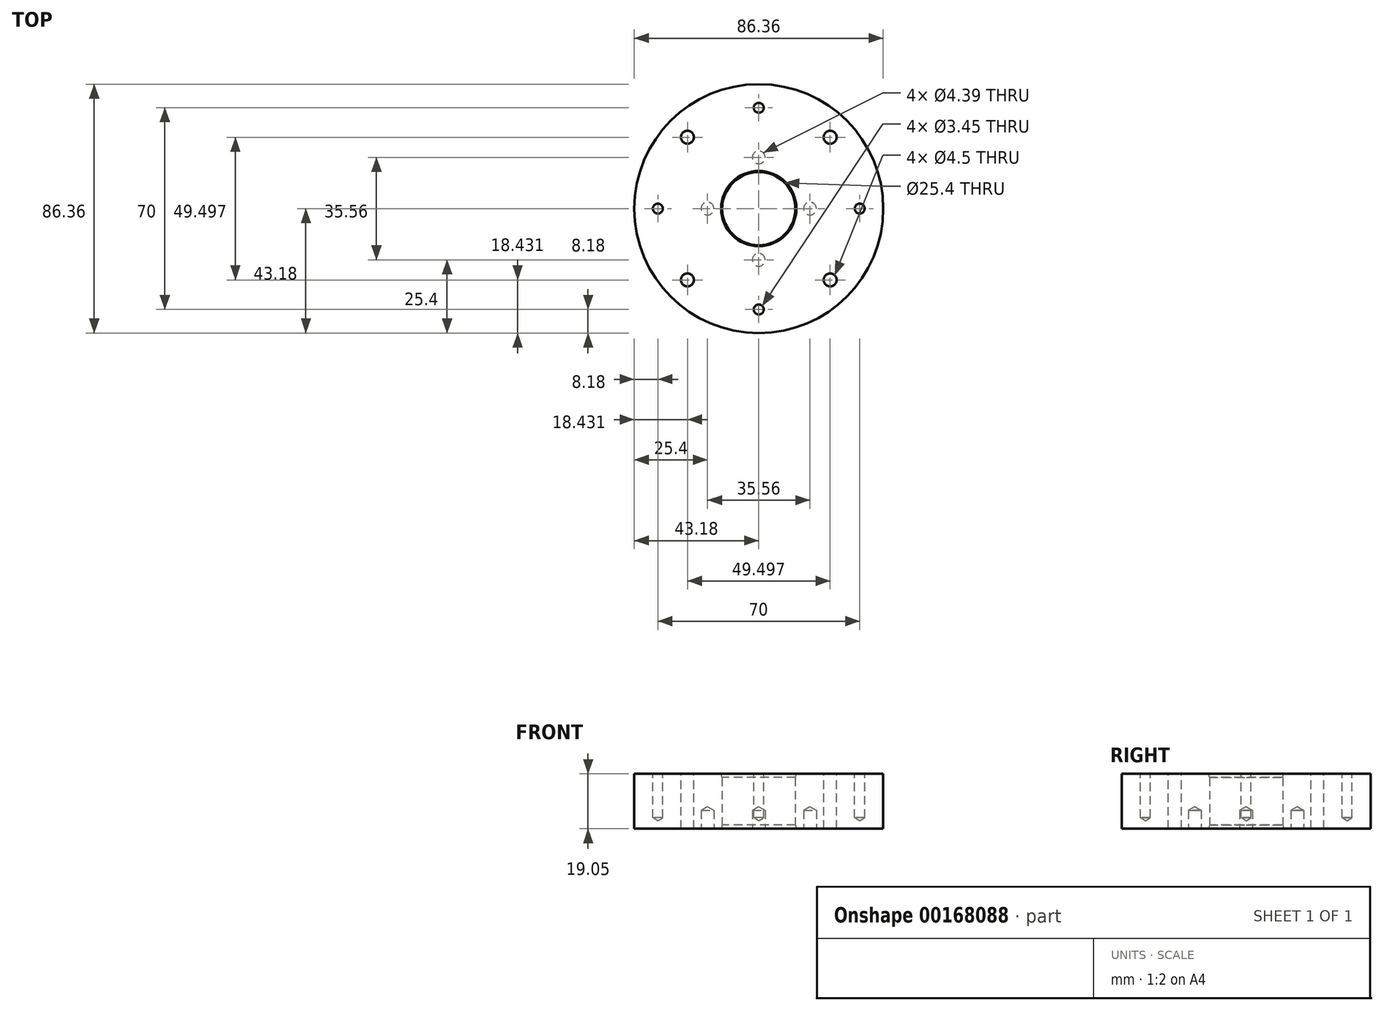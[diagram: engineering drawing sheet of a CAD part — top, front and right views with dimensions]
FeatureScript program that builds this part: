
annotation { "Feature Type Name" : "Feature", "Feature Type Description" : "" }
export const myFeature = defineFeature(function(context is Context, id is Id, definition is map)
    precondition{}
    {
        {
            var Q0;
            Q0=qCreatedBy(makeId("Top.planeOp"),FACE);
            var sketch = newSketch(context, id + "F0", { "sketchPlane" : qUnion([Q0])});
            skCircle(sketch, "E0", {"center": v(0, 0) * mm, "radius": 43.18 * mm});
            skCircle(sketch, "E1", {"center": v(0, 0) * mm, "radius": 12.7 * mm});
            skSolve(sketch);
        }
        {
            var Q0;
            Q0=qSketchRegion(id+"F0",true);
            extrude(context, id + "F1", {"entities" : qUnion([Q0]), "depth" : 19.05 * mm});
        }
        {
            var Q0;
            Q0=makeQuery(id+"F1.opExtrude","CAP_EDGE",EDGE,{"disambiguationData":[OSD([sQuery(id+"F0.wireOp",EDGE,"E1")])],"isStart":false});
            var Q1;
            Q1=makeQuery(id+"F1.opExtrude","CAP_EDGE",EDGE,{"disambiguationData":[OSD([sQuery(id+"F0.wireOp",EDGE,"E1")])],"isStart":true});
            chamfer(context, id + "F2", {"entities" : qUnion([Q0, Q1]), "chamferType" : ChamferType.OFFSET_ANGLE, "width" : 1.27 * mm, "oppositeDirection" : false, "angle" : 15 * degree, "tangentPropagation" : true});
        }
        {
            var Q0;
            Q0=makeQuery(id+"F1.opExtrude","CAP_FACE",FACE,{"disambiguationData":[OSD([sQuery(id+"F0.wireOp",EDGE,"E0"),sQuery(id+"F0.wireOp",EDGE,"E1")])],"isStart":true});
            var sketch = newSketch(context, id + "F3", { "sketchPlane" : qUnion([Q0])});
            skLineSegment(sketch, "E2", {"start": v(0, 0) * mm, "end": v(0, -12.7) * mm, "construction": true});
            skLineSegment(sketch, "E3", {"start": v(0, -12.7) * mm, "end": v(0, -22.86) * mm, "construction": true});
            skLineSegment(sketch, "E4", {"start": v(0, -22.86) * mm, "end": v(0, -12.7) * mm, "construction": true});
            skPoint(sketch, "E5", {"position": v(0, -17.78) * mm});
            skPoint(sketch, "E6.1.0", {"position": v(17.78, 0) * mm});
            skPoint(sketch, "E6.2.0", {"position": v(0, 17.78) * mm});
            skPoint(sketch, "E6.3.0", {"position": v(-17.78, 0) * mm});
            skPoint(sketch, "E6.center", {"position": v(0, 0) * mm});
            skSolve(sketch);
        }
        {
            var Q0;
            Q0=sQuery(id+"F3.wireOp",VERTEX,"E5");
            var Q1;
            Q1=sQuery(id+"F3.wireOp",VERTEX,"E6.3.0");
            var Q2;
            Q2=sQuery(id+"F3.wireOp",VERTEX,"E6.2.0");
            var Q3;
            Q3=sQuery(id+"F3.wireOp",VERTEX,"E6.1.0");
            var Q4;
            Q4=makeQuery(id+"F1.opExtrude","SWEPT_BODY",BODY,{"disambiguationData":[OSD([sQuery(id+"F0.wireOp",EDGE,"E0"),sQuery(id+"F0.wireOp",EDGE,"E1")])]});
            hole(context, id + "F4", {"style" : HoleStyle.SIMPLE, "endStyle" : HoleEndStyle.BLIND, "holeDiameter" : 4.4 * mm, "holeDepth" : 6.35 * mm, "locations" : qUnion([Q0, Q1, Q2, Q3]), "scope" : qUnion([Q4])});
        }
        {
            var Q0;
            Q0=makeQuery(id+"F1.opExtrude","CAP_FACE",FACE,{"disambiguationData":[OSD([sQuery(id+"F0.wireOp",EDGE,"E0"),sQuery(id+"F0.wireOp",EDGE,"E1")])],"isStart":false});
            var sketch = newSketch(context, id + "F5", { "sketchPlane" : qUnion([Q0])});
            skLineSegment(sketch, "E7", {"start": v(0, 0) * mm, "end": v(35, 0) * mm});
            skPoint(sketch, "E8", {"position": v(35, 0) * mm});
            skPoint(sketch, "E9.1.0", {"position": v(0, 35) * mm});
            skPoint(sketch, "E9.2.0", {"position": v(-35, 0) * mm});
            skPoint(sketch, "E9.3.0", {"position": v(0, -35) * mm});
            skPoint(sketch, "E9.center", {"position": v(0, 0) * mm});
            skSolve(sketch);
        }
        {
            var Q0;
            Q0=sQuery(id+"F5.wireOp",VERTEX,"E8");
            var Q1;
            Q1=sQuery(id+"F5.wireOp",VERTEX,"E9.3.0");
            var Q2;
            Q2=sQuery(id+"F5.wireOp",VERTEX,"E9.2.0");
            var Q3;
            Q3=sQuery(id+"F5.wireOp",VERTEX,"E9.1.0");
            var Q4;
            Q4=makeQuery(id+"F1.opExtrude","SWEPT_BODY",BODY,{"disambiguationData":[OSD([sQuery(id+"F0.wireOp",EDGE,"E0"),sQuery(id+"F0.wireOp",EDGE,"E1")])]});
            hole(context, id + "F6", {"style" : HoleStyle.SIMPLE, "endStyle" : HoleEndStyle.BLIND, "standardTappedOrClearance" : lookupTablePath({ "standard" : "ANSI", "engagement" : "75%", "pitch" : "32 tpi", "size" : "#8", "type" : "Tapped" }), "standardBlindInLast" : lookupTablePath({ "standard" : "ANSI", "engagement" : "75%", "pitch" : "32 tpi", "size" : "#8", "type" : "Tapped" }), "holeDiameter" : 3.45 * mm, "holeDepth" : 15.24 * mm, "locations" : qUnion([Q0, Q1, Q2, Q3]), "scope" : qUnion([Q4]), "majorDiameter" : 4.17 * mm});
        }
        {
            var Q0;
            Q0=makeQuery(id+"F1.opExtrude","CAP_FACE",FACE,{"disambiguationData":[OSD([sQuery(id+"F0.wireOp",EDGE,"E0"),sQuery(id+"F0.wireOp",EDGE,"E1")])],"isStart":false});
            var sketch = newSketch(context, id + "F7", { "sketchPlane" : qUnion([Q0])});
            skLineSegment(sketch, "E10", {"start": v(0, 0) * mm, "end": v(24.75, -24.75) * mm, "construction": true});
            skPoint(sketch, "E11", {"position": v(24.75, -24.75) * mm});
            skPoint(sketch, "E12.1.0", {"position": v(24.75, 24.75) * mm});
            skPoint(sketch, "E12.2.0", {"position": v(-24.75, 24.75) * mm});
            skPoint(sketch, "E12.3.0", {"position": v(-24.75, -24.75) * mm});
            skPoint(sketch, "E12.center", {"position": v(0, 0) * mm});
            skSolve(sketch);
        }
        {
            var Q0;
            Q0=sQuery(id+"F7.wireOp",VERTEX,"E11");
            var Q1;
            Q1=sQuery(id+"F7.wireOp",VERTEX,"E12.3.0");
            var Q2;
            Q2=sQuery(id+"F7.wireOp",VERTEX,"E12.2.0");
            var Q3;
            Q3=sQuery(id+"F7.wireOp",VERTEX,"E12.1.0");
            var Q4;
            Q4=makeQuery(id+"F1.opExtrude","SWEPT_BODY",BODY,{"disambiguationData":[OSD([sQuery(id+"F0.wireOp",EDGE,"E0"),sQuery(id+"F0.wireOp",EDGE,"E1")])]});
            hole(context, id + "F8", {"style" : HoleStyle.SIMPLE, "endStyle" : HoleEndStyle.THROUGH, "standardTappedOrClearance" : lookupTablePath({ "standard" : "ANSI", "fit" : "Normal (ASME)", "size" : "#8", "type" : "Clearance" }), "standardBlindInLast" : lookupTablePath({ "fit" : "Free", "standard" : "ANSI", "size" : "#8", "type" : "Clearance" }), "holeDiameter" : 4.5 * mm, "locations" : qUnion([Q0, Q1, Q2, Q3]), "scope" : qUnion([Q4]), "isTappedThrough" : true});
        }
    });
